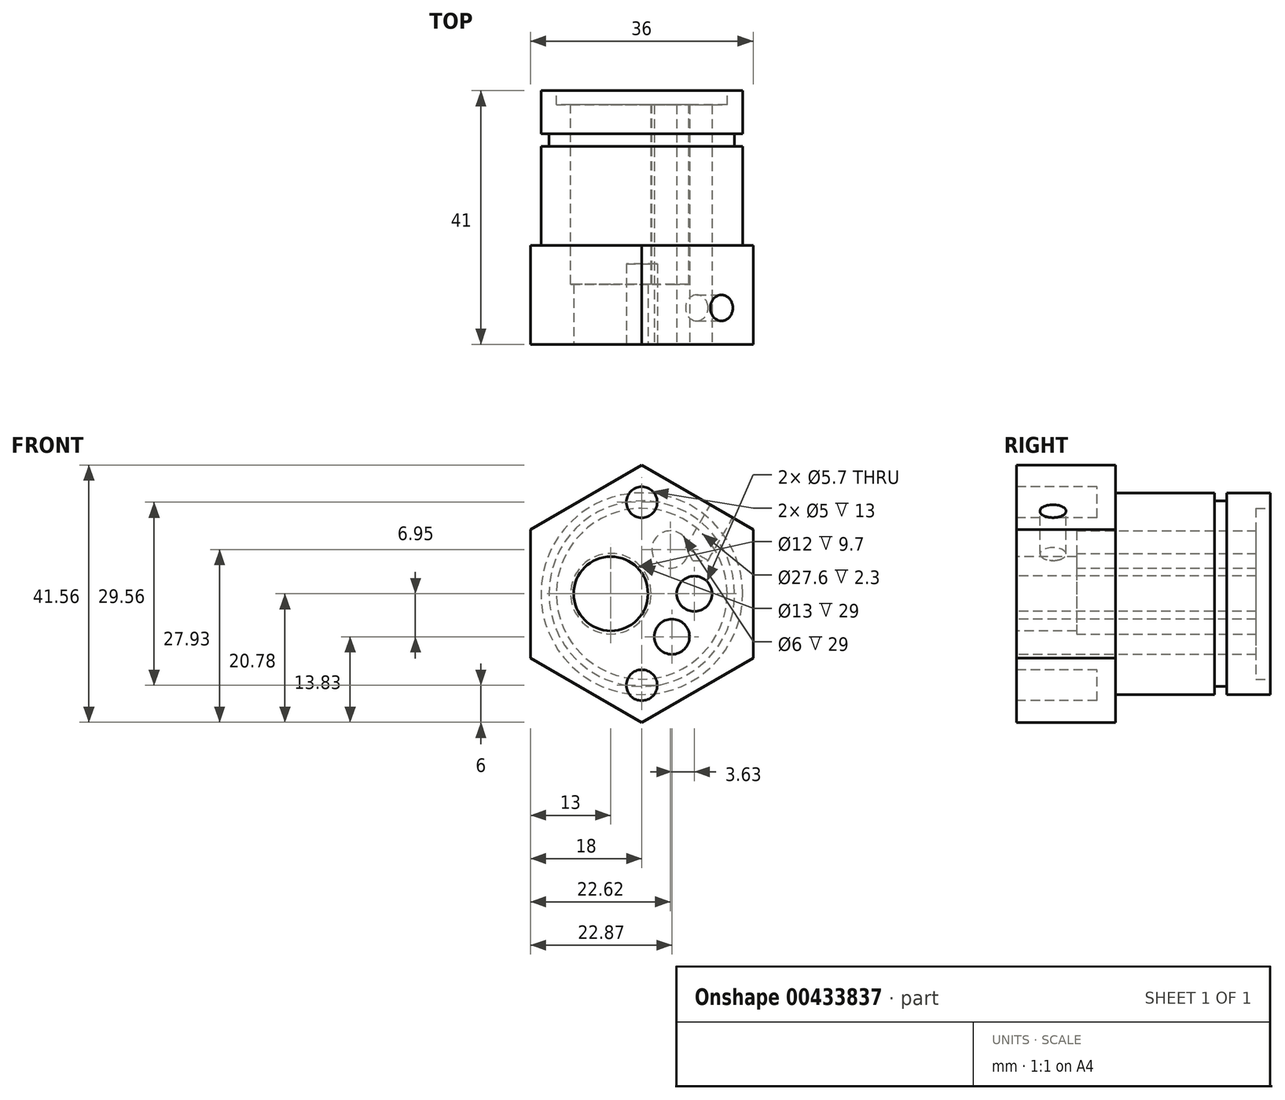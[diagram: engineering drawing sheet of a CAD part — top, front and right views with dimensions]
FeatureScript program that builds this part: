
annotation { "Feature Type Name" : "Feature", "Feature Type Description" : "" }
export const myFeature = defineFeature(function(context is Context, id is Id, definition is map)
    precondition{}
    {
        {
            var Q0;
            Q0=qCreatedBy(makeId("Front.planeOp"),FACE);
            var sketch = newSketch(context, id + "F0", { "sketchPlane" : qUnion([Q0])});
            skCircle(sketch, "E0.cCircle", {"center": v(0, 0) * mm, "radius": 18 * mm, "construction": true});
            skLineSegment(sketch, "E0.0", {"start": v(18, -10.4) * mm, "end": v(0, -20.78) * mm});
            skLineSegment(sketch, "E0.1", {"start": v(0, -20.78) * mm, "end": v(-18, -10.4) * mm});
            skLineSegment(sketch, "E0.2", {"start": v(-18, -10.4) * mm, "end": v(-18, 10.4) * mm});
            skLineSegment(sketch, "E0.3", {"start": v(-18, 10.4) * mm, "end": v(0, 20.78) * mm});
            skLineSegment(sketch, "E0.4", {"start": v(0, 20.78) * mm, "end": v(18, 10.4) * mm});
            skLineSegment(sketch, "E0.5", {"start": v(18, 10.4) * mm, "end": v(18, -10.4) * mm});
            skPoint(sketch, "E0.0.midPoint", {"position": v(9, -15.59) * mm});
            skSolve(sketch);
        }
        {
            var Q0;
            Q0 = qSketchRegion(id + "F0", true);
            extrude(context, id + "F1", {"entities" : qUnion([Q0]), "oppositeDirection" : true, "depth" : 41 * mm});
        }
        {
            var Q0;
            Q0=makeQuery(id+"F1.opExtrude","CAP_FACE",FACE,{"disambiguationData":[OSD([sQuery(id+"F0.wireOp",EDGE,"E0.0"),sQuery(id+"F0.wireOp",EDGE,"E0.1"),sQuery(id+"F0.wireOp",EDGE,"E0.2"),sQuery(id+"F0.wireOp",EDGE,"E0.3"),sQuery(id+"F0.wireOp",EDGE,"E0.4"),sQuery(id+"F0.wireOp",EDGE,"E0.5")])],"isStart":false});
            var sketch = newSketch(context, id + "F2", { "sketchPlane" : qUnion([Q0])});
            skCircle(sketch, "E1", {"center": v(0, 0) * mm, "radius": 24.55 * mm});
            skCircle(sketch, "E2", {"center": v(0, 0) * mm, "radius": 16.3 * mm});
            skSolve(sketch);
        }
        {
            var Q0;
            Q0 = qSketchRegion(id + "F2", true);
            extrude(context, id + "F3", {"entities" : qUnion([Q0]), "operationType" : NewBodyOperationType.REMOVE, "oppositeDirection" : true, "depth" : 25 * mm});
        }
        {
            var Q0;
            Q0=makeQuery(id+"F1.opExtrude","CAP_FACE",FACE,{"disambiguationData":[OSD([sQuery(id+"F0.wireOp",EDGE,"E0.0"),sQuery(id+"F0.wireOp",EDGE,"E0.1"),sQuery(id+"F0.wireOp",EDGE,"E0.2"),sQuery(id+"F0.wireOp",EDGE,"E0.3"),sQuery(id+"F0.wireOp",EDGE,"E0.4"),sQuery(id+"F0.wireOp",EDGE,"E0.5")])],"isStart":false});
            var sketch = newSketch(context, id + "F4", { "sketchPlane" : qUnion([Q0])});
            skCircle(sketch, "E3", {"center": v(0, 0) * mm, "radius": 24.05 * mm});
            skCircle(sketch, "E4", {"center": v(0, 0) * mm, "radius": 15 * mm});
            skSolve(sketch);
        }
        {
            var Q0;
            Q0 = qSketchRegion(id + "F4", true);
            extrude(context, id + "F5", {"entities" : qUnion([Q0]), "operationType" : NewBodyOperationType.REMOVE, "oppositeDirection" : true, "depth" : 9 * mm});
        }
        {
            var Q0;
            Q0=makeQuery(id+"F1.opExtrude","CAP_FACE",FACE,{"disambiguationData":[OSD([sQuery(id+"F0.wireOp",EDGE,"E0.0"),sQuery(id+"F0.wireOp",EDGE,"E0.1"),sQuery(id+"F0.wireOp",EDGE,"E0.2"),sQuery(id+"F0.wireOp",EDGE,"E0.3"),sQuery(id+"F0.wireOp",EDGE,"E0.4"),sQuery(id+"F0.wireOp",EDGE,"E0.5")])],"isStart":false});
            var sketch = newSketch(context, id + "F6", { "sketchPlane" : qUnion([Q0])});
            skCircle(sketch, "E5", {"center": v(0, 0) * mm, "radius": 16.3 * mm});
            skSolve(sketch);
        }
        {
            var Q0;
            Q0 = qSketchRegion(id + "F6", true);
            extrude(context, id + "F7", {"entities" : qUnion([Q0]), "operationType" : NewBodyOperationType.ADD, "oppositeDirection" : true, "depth" : 7 * mm});
        }
        {
            var Q0;
            Q0=makeQuery(id+"F1.opExtrude","CAP_FACE",FACE,{"disambiguationData":[OSD([sQuery(id+"F0.wireOp",EDGE,"E0.0"),sQuery(id+"F0.wireOp",EDGE,"E0.1"),sQuery(id+"F0.wireOp",EDGE,"E0.2"),sQuery(id+"F0.wireOp",EDGE,"E0.3"),sQuery(id+"F0.wireOp",EDGE,"E0.4"),sQuery(id+"F0.wireOp",EDGE,"E0.5")])],"isStart":true});
            var sketch = newSketch(context, id + "F8", { "sketchPlane" : qUnion([Q0])});
            skCircle(sketch, "E6", {"center": v(4.87, -6.95) * mm, "radius": 2.85 * mm});
            skCircle(sketch, "E7", {"center": v(8.5, 0) * mm, "radius": 2.85 * mm});
            skSolve(sketch);
        }
        {
            var Q0;
            Q0 = qSketchRegion(id + "F8", true);
            extrude(context, id + "F9", {"entities" : qUnion([Q0]), "operationType" : NewBodyOperationType.REMOVE, "endBound" : BoundingType.THROUGH_ALL, "oppositeDirection" : true, "depth" : 25 * mm});
        }
        {
            var Q0;
            Q0=makeQuery(id+"F7.boolean.opBoolean","MERGE",FACE,{"derivedFrom":[makeQuery(id+"F1.opExtrude","CAP_FACE",FACE,{"disambiguationData":[OSD([sQuery(id+"F0.wireOp",EDGE,"E0.0"),sQuery(id+"F0.wireOp",EDGE,"E0.1"),sQuery(id+"F0.wireOp",EDGE,"E0.2"),sQuery(id+"F0.wireOp",EDGE,"E0.3"),sQuery(id+"F0.wireOp",EDGE,"E0.4"),sQuery(id+"F0.wireOp",EDGE,"E0.5")])],"isStart":false}),makeQuery(id+"F7.opExtrude","CAP_FACE",FACE,{"disambiguationData":[OSD([sQuery(id+"F6.wireOp",EDGE,"E5")])],"isStart":true})]});
            var sketch = newSketch(context, id + "F10", { "sketchPlane" : qUnion([Q0])});
            skCircle(sketch, "E8", {"center": v(0, 0) * mm, "radius": 13.8 * mm});
            skSolve(sketch);
        }
        {
            var Q0;
            Q0 = qSketchRegion(id + "F10", true);
            extrude(context, id + "F11", {"entities" : qUnion([Q0]), "operationType" : NewBodyOperationType.REMOVE, "oppositeDirection" : true, "depth" : 2.3 * mm});
        }
        {
            var Q0;
            Q0=makeQuery(id+"F1.opExtrude","CAP_FACE",FACE,{"disambiguationData":[OSD([sQuery(id+"F0.wireOp",EDGE,"E0.0"),sQuery(id+"F0.wireOp",EDGE,"E0.1"),sQuery(id+"F0.wireOp",EDGE,"E0.2"),sQuery(id+"F0.wireOp",EDGE,"E0.3"),sQuery(id+"F0.wireOp",EDGE,"E0.4"),sQuery(id+"F0.wireOp",EDGE,"E0.5")])],"isStart":true});
            var sketch = newSketch(context, id + "F12", { "sketchPlane" : qUnion([Q0])});
            skCircle(sketch, "E9", {"center": v(-5, 0) * mm, "radius": 6 * mm});
            skSolve(sketch);
        }
        {
            var Q0;
            Q0 = qSketchRegion(id + "F12", true);
            extrude(context, id + "F13", {"entities" : qUnion([Q0]), "operationType" : NewBodyOperationType.REMOVE, "endBound" : BoundingType.THROUGH_ALL, "oppositeDirection" : true, "depth" : 25 * mm});
        }
        {
            var Q0;
            Q0=makeQuery(id+"F11.boolean.opBoolean","COPY",FACE,{"derivedFrom":makeQuery(id+"F11.opExtrude","CAP_FACE",FACE,{"disambiguationData":[OSD([sQuery(id+"F10.wireOp",EDGE,"E8")])],"isStart":false})});
            var sketch = newSketch(context, id + "F14", { "sketchPlane" : qUnion([Q0])});
            skCircle(sketch, "E10", {"center": v(5, 0) * mm, "radius": 6.5 * mm});
            skSolve(sketch);
        }
        {
            var Q0;
            Q0 = qSketchRegion(id + "F14", true);
            extrude(context, id + "F15", {"entities" : qUnion([Q0]), "operationType" : NewBodyOperationType.REMOVE, "oppositeDirection" : true, "depth" : 29 * mm});
        }
        {
            var Q0;
            Q0=makeQuery(id+"F1.opExtrude","CAP_FACE",FACE,{"disambiguationData":[OSD([sQuery(id+"F0.wireOp",EDGE,"E0.0"),sQuery(id+"F0.wireOp",EDGE,"E0.1"),sQuery(id+"F0.wireOp",EDGE,"E0.2"),sQuery(id+"F0.wireOp",EDGE,"E0.3"),sQuery(id+"F0.wireOp",EDGE,"E0.4"),sQuery(id+"F0.wireOp",EDGE,"E0.5")])],"isStart":true});
            var sketch = newSketch(context, id + "F16", { "sketchPlane" : qUnion([Q0])});
            skCircle(sketch, "E11", {"center": v(0, 14.78) * mm, "radius": 2.5 * mm});
            skSolve(sketch);
        }
        {
            var Q0;
            Q0 = qSketchRegion(id + "F16", true);
            extrude(context, id + "F17", {"entities" : qUnion([Q0]), "operationType" : NewBodyOperationType.REMOVE, "oppositeDirection" : true, "depth" : 13 * mm});
        }
        {
            var Q0;
            Q0=makeQuery(id+"F1.opExtrude","CAP_FACE",FACE,{"disambiguationData":[OSD([sQuery(id+"F0.wireOp",EDGE,"E0.0"),sQuery(id+"F0.wireOp",EDGE,"E0.1"),sQuery(id+"F0.wireOp",EDGE,"E0.2"),sQuery(id+"F0.wireOp",EDGE,"E0.3"),sQuery(id+"F0.wireOp",EDGE,"E0.4"),sQuery(id+"F0.wireOp",EDGE,"E0.5")])],"isStart":true});
            var sketch = newSketch(context, id + "F18", { "sketchPlane" : qUnion([Q0])});
            skCircle(sketch, "E12", {"center": v(0, -14.78) * mm, "radius": 2.5 * mm});
            skSolve(sketch);
        }
        {
            var Q0;
            Q0 = qSketchRegion(id + "F18", true);
            extrude(context, id + "F19", {"entities" : qUnion([Q0]), "operationType" : NewBodyOperationType.REMOVE, "oppositeDirection" : true, "depth" : 13 * mm});
        }
        {
            var Q0;
            Q0=makeQuery(id+"F1.opExtrude","SWEPT_FACE",FACE,{"disambiguationData":[OSD([sQuery(id+"F0.wireOp",EDGE,"E0.4")])]});
            var sketch = newSketch(context, id + "F20", { "sketchPlane" : qUnion([Q0])});
            skCircle(sketch, "E13", {"center": v(4.5, 5.9) * mm, "radius": 2.1 * mm});
            skSolve(sketch);
        }
        {
            var Q0;
            Q0=sQuery(id+"F20.wireOp",VERTEX,"E13.center");
            var Q1;
            Q1=makeQuery(id+"F1.opExtrude","SWEPT_BODY",BODY,{"disambiguationData":[OSD([sQuery(id+"F0.wireOp",EDGE,"E0.0"),sQuery(id+"F0.wireOp",EDGE,"E0.1"),sQuery(id+"F0.wireOp",EDGE,"E0.2"),sQuery(id+"F0.wireOp",EDGE,"E0.3"),sQuery(id+"F0.wireOp",EDGE,"E0.4"),sQuery(id+"F0.wireOp",EDGE,"E0.5")])]});
            hole(context, id + "F21", {"style" : HoleStyle.SIMPLE, "endStyle" : HoleEndStyle.BLIND, "holeDiameter" : 4.2 * mm, "holeDepth" : 8 * mm, "isTappedThrough" : true, "tappedDepth" : 12 * mm, "tapClearance" : 3, "locations" : qUnion([Q0]), "scope" : qUnion([Q1])});
        }
        {
            var Q0;
            Q0=makeQuery(id+"F11.boolean.opBoolean","COPY",FACE,{"derivedFrom":makeQuery(id+"F11.opExtrude","CAP_FACE",FACE,{"disambiguationData":[OSD([sQuery(id+"F10.wireOp",EDGE,"E8")])],"isStart":false})});
            var sketch = newSketch(context, id + "F22", { "sketchPlane" : qUnion([Q0])});
            skCircle(sketch, "E14", {"center": v(-4.62, 7.15) * mm, "radius": 3 * mm});
            skSolve(sketch);
        }
        {
            var Q0;
            Q0 = qSketchRegion(id + "F22", true);
            extrude(context, id + "F23", {"entities" : qUnion([Q0]), "operationType" : NewBodyOperationType.REMOVE, "oppositeDirection" : true, "depth" : 29 * mm});
        }
    });
